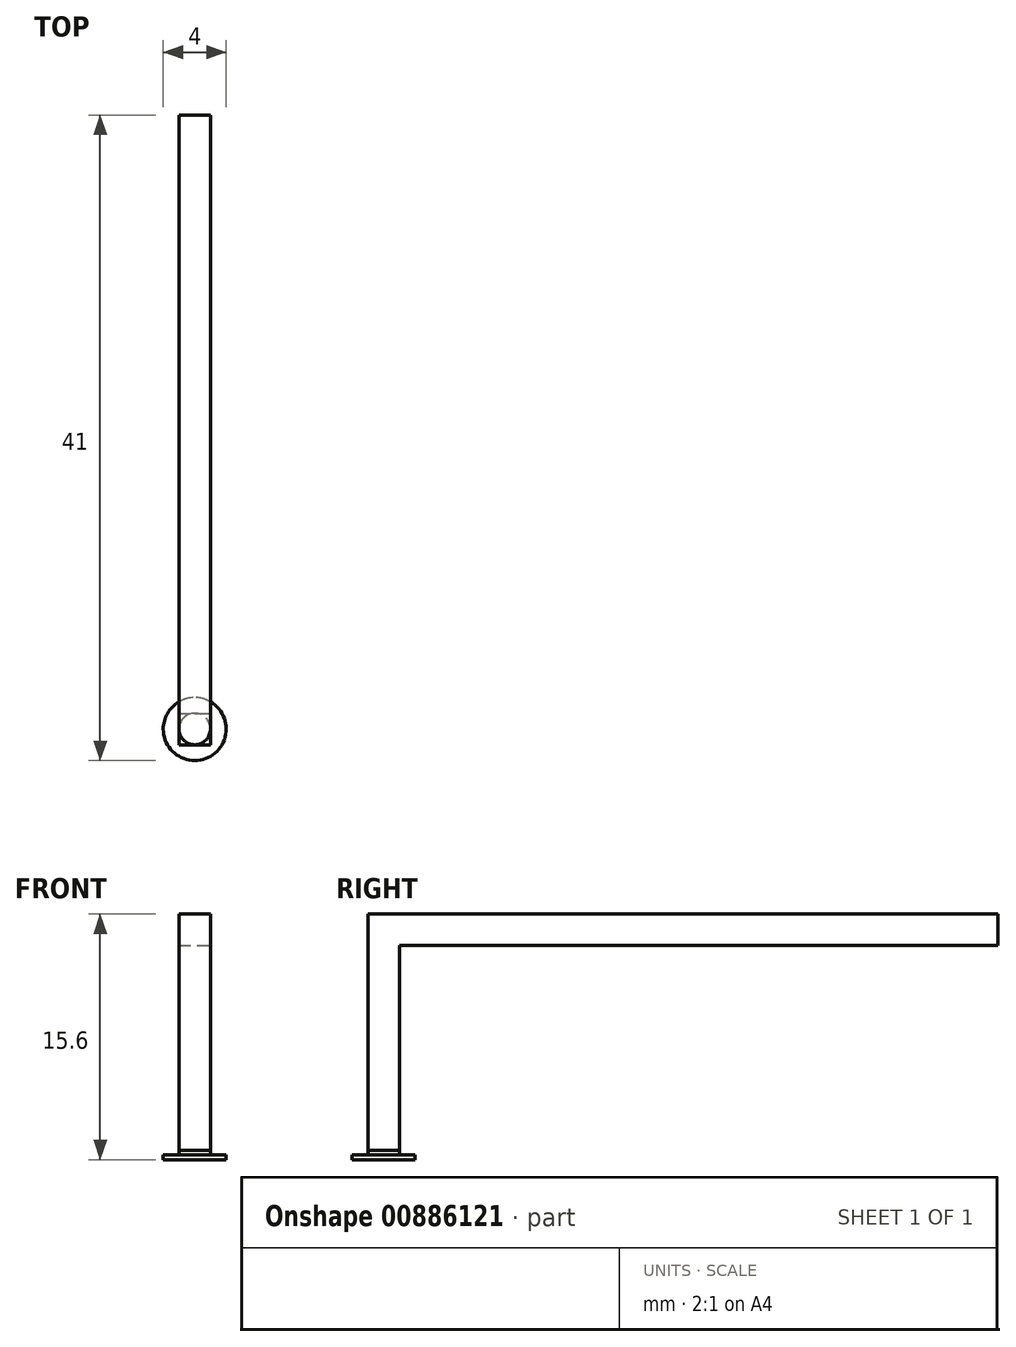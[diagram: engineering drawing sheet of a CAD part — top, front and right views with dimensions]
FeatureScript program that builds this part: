
annotation { "Feature Type Name" : "Feature", "Feature Type Description" : "" }
export const myFeature = defineFeature(function(context is Context, id is Id, definition is map)
    precondition{}
    {
        {
            var Q0;
            Q0=qCreatedBy(makeId("Front.planeOp"),FACE);
            var sketch = newSketch(context, id + "F0", { "sketchPlane" : qUnion([Q0])});
            skLineSegment(sketch, "E0.bottom", {"start": v(0, 0) * mm, "end": v(2, 0) * mm});
            skLineSegment(sketch, "E0.top", {"start": v(0, -2) * mm, "end": v(2, -2) * mm});
            skLineSegment(sketch, "E0.left", {"start": v(0, 0) * mm, "end": v(0, -2) * mm});
            skLineSegment(sketch, "E0.right", {"start": v(2, 0) * mm, "end": v(2, -2) * mm});
            skSolve(sketch);
        }
        {
            var Q0;
            Q0 = qSketchRegion(id + "F0", true);
            extrude(context, id + "F1", {"entities" : qUnion([Q0]), "depth" : 40 * mm, "offsetDistance" : 25 * mm});
        }
        {
            var Q0;
            Q0=qCreatedBy(makeId("Top.planeOp"),FACE);
            var sketch = newSketch(context, id + "F2", { "sketchPlane" : qUnion([Q0])});
            skLineSegment(sketch, "E1.bottom", {"start": v(0, -40) * mm, "end": v(2, -40) * mm});
            skLineSegment(sketch, "E1.top", {"start": v(0, -38) * mm, "end": v(2, -38) * mm});
            skLineSegment(sketch, "E1.left", {"start": v(0, -40) * mm, "end": v(0, -38) * mm});
            skLineSegment(sketch, "E1.right", {"start": v(2, -40) * mm, "end": v(2, -38) * mm});
            skSolve(sketch);
        }
        {
            var Q0;
            Q0 = qSketchRegion(id + "F2", true);
            extrude(context, id + "F3", {"entities" : qUnion([Q0]), "operationType" : NewBodyOperationType.ADD, "depth" : -15 * mm, "offsetDistance" : 25 * mm});
        }
        {
            var Q0;
            Q0=makeQuery(id+"F3.opExtrude","CAP_FACE",FACE,{"disambiguationData":[OSD([sQuery(id+"F2.wireOp",EDGE,"E1.bottom"),sQuery(id+"F2.wireOp",EDGE,"E1.top"),sQuery(id+"F2.wireOp",EDGE,"E1.left"),sQuery(id+"F2.wireOp",EDGE,"E1.right")])],"isStart":false});
            var sketch = newSketch(context, id + "F4", { "sketchPlane" : qUnion([Q0])});
            skCircle(sketch, "E2", {"center": v(1, 39) * mm, "radius": 1 * mm});
            skPoint(sketch, "E2.first.point", {"position": v(1, 40) * mm});
            skPoint(sketch, "E2.second.point", {"position": v(1, 38) * mm});
            skPoint(sketch, "E2.third.point", {"position": v(0, 39) * mm});
            skSolve(sketch);
        }
        {
            var Q0;
            Q0 = qSketchRegion(id + "F4", true);
            extrude(context, id + "F5", {"entities" : qUnion([Q0]), "operationType" : NewBodyOperationType.ADD, "depth" : 0.3 * mm, "offsetDistance" : 25 * mm});
        }
        {
            var Q0;
            Q0=makeQuery(id+"F5.opExtrude","CAP_FACE",FACE,{"disambiguationData":[OSD([sQuery(id+"F4.wireOp",EDGE,"E2")])],"isStart":false});
            var sketch = newSketch(context, id + "F6", { "sketchPlane" : qUnion([Q0])});
            skCircle(sketch, "E3", {"center": v(1, 39) * mm, "radius": 2 * mm});
            skSolve(sketch);
        }
        {
            var Q0;
            Q0 = qSketchRegion(id + "F6", true);
            extrude(context, id + "F7", {"entities" : qUnion([Q0]), "operationType" : NewBodyOperationType.ADD, "depth" : 0.3 * mm, "offsetDistance" : 25 * mm});
        }
    });
